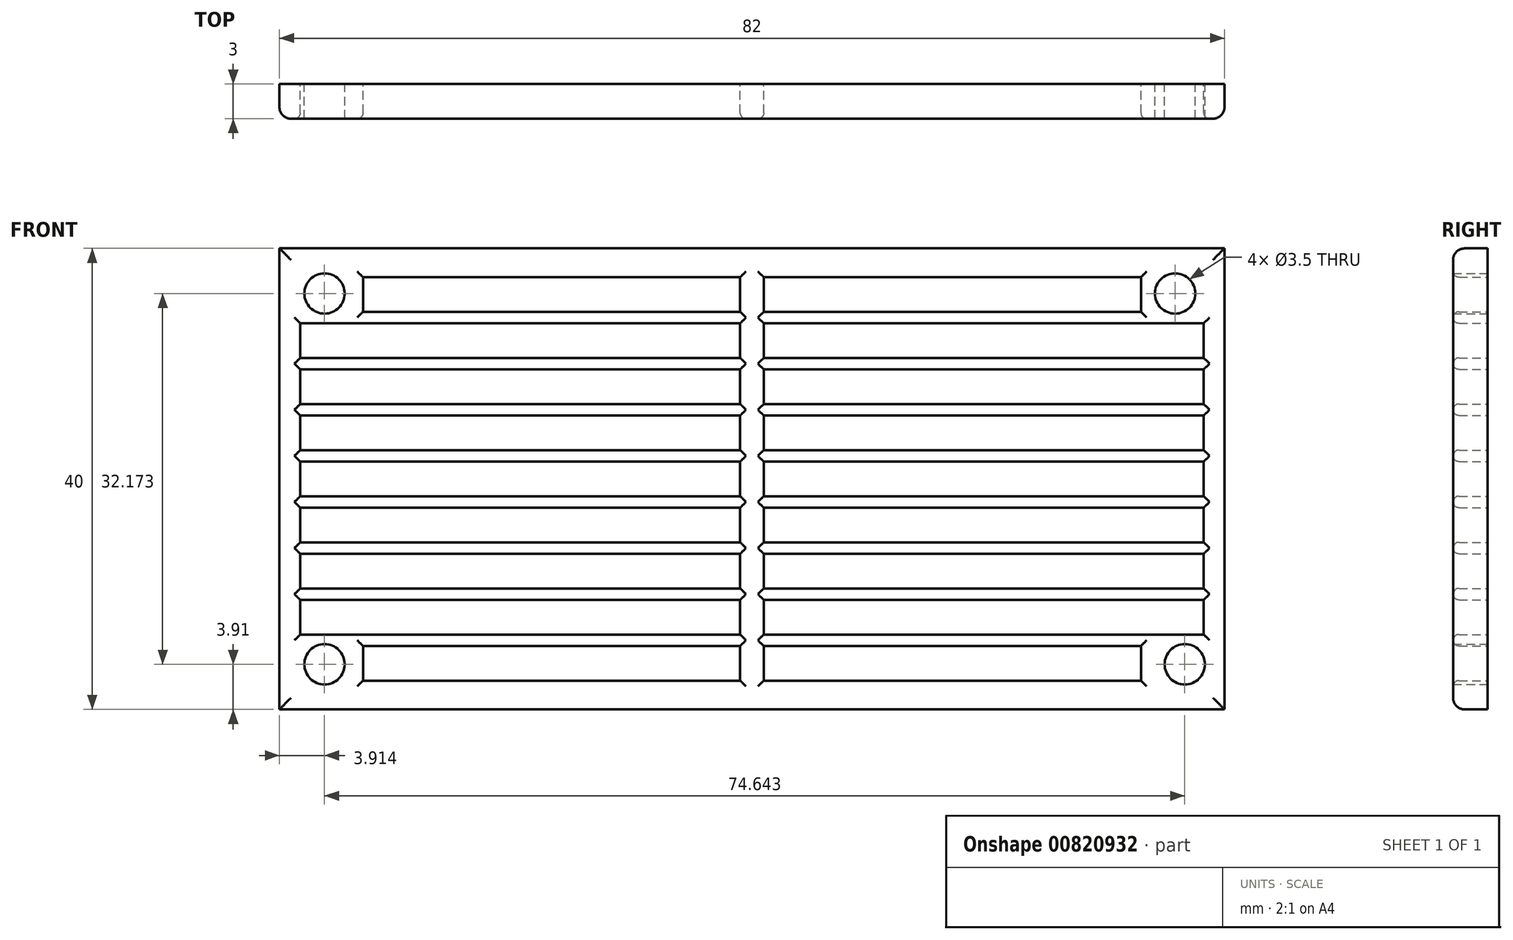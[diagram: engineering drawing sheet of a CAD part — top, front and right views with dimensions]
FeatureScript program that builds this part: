
annotation { "Feature Type Name" : "Feature", "Feature Type Description" : "" }
export const myFeature = defineFeature(function(context is Context, id is Id, definition is map)
    precondition{}
    {
        {
            var Q0;
            Q0=qCreatedBy(makeId("Front.planeOp"),FACE);
            var sketch = newSketch(context, id + "F0", { "sketchPlane" : qUnion([Q0])});
            skLineSegment(sketch, "E0.bottom", {"start": v(-95.77, 58.49) * mm, "end": v(-55.77, 58.49) * mm, "construction": true});
            skLineSegment(sketch, "E0.top", {"start": v(-95.77, 18.49) * mm, "end": v(-55.77, 18.49) * mm, "construction": true});
            skLineSegment(sketch, "E0.left", {"start": v(-95.77, 58.49) * mm, "end": v(-95.77, 18.49) * mm, "construction": true});
            skPoint(sketch, "E0.middle", {"position": v(-75.77, 38.49) * mm});
            skLineSegment(sketch, "E1.left", {"start": v(-13.77, 58.96) * mm, "end": v(-13.77, 18.96) * mm, "construction": true});
            skPoint(sketch, "E1.middle", {"position": v(-33.77, 38.49) * mm});
            skCircle(sketch, "E2", {"center": v(-91.86, 54.57) * mm, "radius": 1.75 * mm});
            skCircle(sketch, "E3", {"center": v(-91.86, 22.4) * mm, "radius": 1.75 * mm});
            skCircle(sketch, "E4", {"center": v(-18.05, 54.57) * mm, "radius": 1.75 * mm});
            skCircle(sketch, "E5", {"center": v(-17.21, 22.4) * mm, "radius": 1.75 * mm});
            skPoint(sketch, "E6.middle", {"position": v(-54.77, 38.49) * mm});
            skPoint(sketch, "E7.centerSnap0", {"position": v(-13.77, 38.96) * mm});
            skLineSegment(sketch, "E8.bottom", {"start": v(-95.77, 58.49) * mm, "end": v(-13.77, 58.49) * mm});
            skLineSegment(sketch, "E8.top", {"start": v(-95.77, 18.49) * mm, "end": v(-13.77, 18.49) * mm});
            skLineSegment(sketch, "E8.left", {"start": v(-95.77, 58.49) * mm, "end": v(-95.77, 18.49) * mm});
            skLineSegment(sketch, "E8.right", {"start": v(-13.77, 58.49) * mm, "end": v(-13.77, 18.49) * mm});
            skLineSegment(sketch, "E9.bottom", {"start": v(-15.57, 39.99) * mm, "end": v(-93.96, 39.99) * mm});
            skLineSegment(sketch, "E9.top", {"start": v(-15.57, 36.99) * mm, "end": v(-93.96, 36.99) * mm});
            skLineSegment(sketch, "E9.left", {"start": v(-15.57, 39.99) * mm, "end": v(-15.57, 36.99) * mm});
            skLineSegment(sketch, "E9.right", {"start": v(-93.96, 39.99) * mm, "end": v(-93.96, 36.99) * mm});
            skLineSegment(sketch, "E10.bottom", {"start": v(-15.57, 35.99) * mm, "end": v(-93.96, 35.99) * mm});
            skLineSegment(sketch, "E10.top", {"start": v(-15.57, 32.99) * mm, "end": v(-93.96, 32.99) * mm});
            skLineSegment(sketch, "E10.left", {"start": v(-15.57, 35.99) * mm, "end": v(-15.57, 32.99) * mm});
            skLineSegment(sketch, "E10.right", {"start": v(-93.96, 35.99) * mm, "end": v(-93.96, 32.99) * mm});
            skPoint(sketch, "E10.middle", {"position": v(-54.77, 34.49) * mm});
            skPoint(sketch, "E10.middle.positionSnap0", {"position": v(-54.77, 36.99) * mm});
            skPoint(sketch, "E10.centerSnap0", {"position": v(-54.77, 36.99) * mm});
            skLineSegment(sketch, "E11.bottom", {"start": v(-15.57, 31.99) * mm, "end": v(-93.96, 31.99) * mm});
            skLineSegment(sketch, "E11.top", {"start": v(-15.57, 28.99) * mm, "end": v(-93.96, 28.99) * mm});
            skLineSegment(sketch, "E11.left", {"start": v(-15.57, 31.99) * mm, "end": v(-15.57, 28.99) * mm});
            skLineSegment(sketch, "E11.right", {"start": v(-93.96, 31.99) * mm, "end": v(-93.96, 28.99) * mm});
            skPoint(sketch, "E11.middle", {"position": v(-54.77, 30.49) * mm});
            skPoint(sketch, "E11.middle.positionSnap0", {"position": v(-54.77, 32.99) * mm});
            skPoint(sketch, "E11.centerSnap0", {"position": v(-54.77, 32.99) * mm});
            skLineSegment(sketch, "E12.bottom", {"start": v(-15.57, 27.99) * mm, "end": v(-93.96, 27.99) * mm});
            skLineSegment(sketch, "E12.top", {"start": v(-15.57, 24.99) * mm, "end": v(-93.96, 24.99) * mm});
            skLineSegment(sketch, "E12.left", {"start": v(-15.57, 27.99) * mm, "end": v(-15.57, 24.99) * mm});
            skLineSegment(sketch, "E12.right", {"start": v(-93.96, 27.99) * mm, "end": v(-93.96, 24.99) * mm});
            skPoint(sketch, "E12.middle", {"position": v(-54.77, 26.49) * mm});
            skPoint(sketch, "E12.middle.positionSnap0", {"position": v(-54.77, 28.99) * mm});
            skPoint(sketch, "E12.centerSnap0", {"position": v(-54.77, 28.99) * mm});
            skLineSegment(sketch, "E13.bottom", {"start": v(-15.57, 40.99) * mm, "end": v(-93.96, 40.99) * mm});
            skLineSegment(sketch, "E13.top", {"start": v(-15.57, 43.99) * mm, "end": v(-93.96, 43.99) * mm});
            skLineSegment(sketch, "E13.left", {"start": v(-15.57, 40.99) * mm, "end": v(-15.57, 43.99) * mm});
            skLineSegment(sketch, "E13.right", {"start": v(-93.96, 40.99) * mm, "end": v(-93.96, 43.99) * mm});
            skPoint(sketch, "E13.middle", {"position": v(-54.77, 42.49) * mm});
            skLineSegment(sketch, "E14.bottom", {"start": v(-15.57, 44.99) * mm, "end": v(-93.96, 44.99) * mm});
            skLineSegment(sketch, "E14.top", {"start": v(-15.57, 47.99) * mm, "end": v(-93.96, 47.99) * mm});
            skLineSegment(sketch, "E14.left", {"start": v(-15.57, 44.99) * mm, "end": v(-15.57, 47.99) * mm});
            skLineSegment(sketch, "E14.right", {"start": v(-93.96, 44.99) * mm, "end": v(-93.96, 47.99) * mm});
            skPoint(sketch, "E14.middle", {"position": v(-54.77, 46.49) * mm});
            skPoint(sketch, "E14.middle.positionSnap0", {"position": v(-54.77, 43.99) * mm});
            skPoint(sketch, "E14.centerSnap0", {"position": v(-54.77, 43.99) * mm});
            skLineSegment(sketch, "E15.bottom", {"start": v(-15.57, 48.99) * mm, "end": v(-93.96, 48.99) * mm});
            skLineSegment(sketch, "E15.top", {"start": v(-15.57, 51.99) * mm, "end": v(-93.96, 51.99) * mm});
            skLineSegment(sketch, "E15.left", {"start": v(-15.57, 48.99) * mm, "end": v(-15.57, 51.99) * mm});
            skLineSegment(sketch, "E15.right", {"start": v(-93.96, 48.99) * mm, "end": v(-93.96, 51.99) * mm});
            skPoint(sketch, "E15.middle", {"position": v(-54.77, 50.49) * mm});
            skLineSegment(sketch, "E16.bottom", {"start": v(-21.02, 52.99) * mm, "end": v(-88.52, 52.99) * mm});
            skLineSegment(sketch, "E16.top", {"start": v(-21.02, 55.99) * mm, "end": v(-88.52, 55.99) * mm});
            skLineSegment(sketch, "E16.left", {"start": v(-21.02, 52.99) * mm, "end": v(-21.02, 55.99) * mm});
            skLineSegment(sketch, "E16.right", {"start": v(-88.52, 52.99) * mm, "end": v(-88.52, 55.99) * mm});
            skPoint(sketch, "E16.middle", {"position": v(-54.77, 54.49) * mm});
            skLineSegment(sketch, "E17.bottom", {"start": v(-21.02, 20.99) * mm, "end": v(-88.52, 20.99) * mm});
            skLineSegment(sketch, "E17.top", {"start": v(-21.02, 23.99) * mm, "end": v(-88.52, 23.99) * mm});
            skLineSegment(sketch, "E17.left", {"start": v(-21.02, 20.99) * mm, "end": v(-21.02, 23.99) * mm});
            skLineSegment(sketch, "E17.right", {"start": v(-88.52, 20.99) * mm, "end": v(-88.52, 23.99) * mm});
            skPoint(sketch, "E17.middle", {"position": v(-54.77, 22.49) * mm});
            skPoint(sketch, "E17.middle.positionSnap0", {"position": v(-54.77, 24.99) * mm});
            skPoint(sketch, "E17.centerSnap0", {"position": v(-54.77, 24.99) * mm});
            skLineSegment(sketch, "E18.bottom", {"start": v(-53.74, 20.99) * mm, "end": v(-55.8, 20.99) * mm});
            skLineSegment(sketch, "E18.top", {"start": v(-53.74, 55.99) * mm, "end": v(-55.8, 55.99) * mm});
            skLineSegment(sketch, "E18.left", {"start": v(-53.74, 20.99) * mm, "end": v(-53.74, 55.99) * mm});
            skLineSegment(sketch, "E18.right", {"start": v(-55.8, 20.99) * mm, "end": v(-55.8, 55.99) * mm});
            skSolve(sketch);
        }
        {
            var Q0;
            Q0=makeQuery(id+"F0.imprint","IMPRINT",FACE,{"disambiguationData":[TD([[makeQuery(id+"F0.imprint","IMPRINT",EDGE,{"derivedFrom":sQuery(id+"F0.wireOp",EDGE,"E2")}),-1.0]])]});
            var Q1;
            {var subQ0=sQuery(id+"F0.wireOp",EDGE,"E18.right");var subQ1=sQuery(id+"F0.wireOp",EDGE,"E16.bottom");var subQ2=makeQuery(id+"F0.imprint","INTERSECT",VERTEX,{"derivedFrom":[subQ1,subQ0]});Q1=makeQuery(id+"F0.imprint","IMPRINT",FACE,{"disambiguationData":[TD([[makeQuery(id+"F0.imprint","IMPRINT",EDGE,{"disambiguationData":[TD([[subQ2,1.0]])],"derivedFrom":subQ1}),-1.0]])]});}
            var Q2;
            {var subQ0=sQuery(id+"F0.wireOp",EDGE,"E18.right");var subQ1=sQuery(id+"F0.wireOp",EDGE,"E15.top");var subQ2=makeQuery(id+"F0.imprint","INTERSECT",VERTEX,{"derivedFrom":[subQ1,subQ0]});Q2=makeQuery(id+"F0.imprint","IMPRINT",FACE,{"disambiguationData":[TD([[makeQuery(id+"F0.imprint","IMPRINT",EDGE,{"disambiguationData":[TD([[subQ2,1.0]])],"derivedFrom":subQ1}),-1.0]])]});}
            var Q3;
            {var subQ0=sQuery(id+"F0.wireOp",EDGE,"E18.right");var subQ1=sQuery(id+"F0.wireOp",EDGE,"E15.bottom");var subQ2=makeQuery(id+"F0.imprint","INTERSECT",VERTEX,{"derivedFrom":[subQ1,subQ0]});Q3=makeQuery(id+"F0.imprint","IMPRINT",FACE,{"disambiguationData":[TD([[makeQuery(id+"F0.imprint","IMPRINT",EDGE,{"disambiguationData":[TD([[subQ2,1.0]])],"derivedFrom":subQ1}),-1.0]])]});}
            var Q4;
            {var subQ0=sQuery(id+"F0.wireOp",EDGE,"E18.right");var subQ1=sQuery(id+"F0.wireOp",EDGE,"E14.top");var subQ2=makeQuery(id+"F0.imprint","INTERSECT",VERTEX,{"derivedFrom":[subQ1,subQ0]});Q4=makeQuery(id+"F0.imprint","IMPRINT",FACE,{"disambiguationData":[TD([[makeQuery(id+"F0.imprint","IMPRINT",EDGE,{"disambiguationData":[TD([[subQ2,1.0]])],"derivedFrom":subQ1}),-1.0]])]});}
            var Q5;
            {var subQ0=sQuery(id+"F0.wireOp",EDGE,"E18.right");var subQ1=sQuery(id+"F0.wireOp",EDGE,"E14.bottom");var subQ2=makeQuery(id+"F0.imprint","INTERSECT",VERTEX,{"derivedFrom":[subQ1,subQ0]});Q5=makeQuery(id+"F0.imprint","IMPRINT",FACE,{"disambiguationData":[TD([[makeQuery(id+"F0.imprint","IMPRINT",EDGE,{"disambiguationData":[TD([[subQ2,1.0]])],"derivedFrom":subQ1}),-1.0]])]});}
            var Q6;
            {var subQ0=sQuery(id+"F0.wireOp",EDGE,"E18.right");var subQ1=sQuery(id+"F0.wireOp",EDGE,"E13.top");var subQ2=makeQuery(id+"F0.imprint","INTERSECT",VERTEX,{"derivedFrom":[subQ1,subQ0]});Q6=makeQuery(id+"F0.imprint","IMPRINT",FACE,{"disambiguationData":[TD([[makeQuery(id+"F0.imprint","IMPRINT",EDGE,{"disambiguationData":[TD([[subQ2,1.0]])],"derivedFrom":subQ1}),-1.0]])]});}
            var Q7;
            {var subQ0=sQuery(id+"F0.wireOp",EDGE,"E18.right");var subQ1=sQuery(id+"F0.wireOp",EDGE,"E13.bottom");var subQ2=makeQuery(id+"F0.imprint","INTERSECT",VERTEX,{"derivedFrom":[subQ1,subQ0]});Q7=makeQuery(id+"F0.imprint","IMPRINT",FACE,{"disambiguationData":[TD([[makeQuery(id+"F0.imprint","IMPRINT",EDGE,{"disambiguationData":[TD([[subQ2,1.0]])],"derivedFrom":subQ1}),-1.0]])]});}
            var Q8;
            {var subQ0=sQuery(id+"F0.wireOp",EDGE,"E18.right");var subQ1=sQuery(id+"F0.wireOp",EDGE,"E9.bottom");var subQ2=makeQuery(id+"F0.imprint","INTERSECT",VERTEX,{"derivedFrom":[subQ1,subQ0]});Q8=makeQuery(id+"F0.imprint","IMPRINT",FACE,{"disambiguationData":[TD([[makeQuery(id+"F0.imprint","IMPRINT",EDGE,{"disambiguationData":[TD([[subQ2,1.0]])],"derivedFrom":subQ1}),-1.0]])]});}
            var Q9;
            {var subQ0=sQuery(id+"F0.wireOp",EDGE,"E18.right");var subQ1=sQuery(id+"F0.wireOp",EDGE,"E9.bottom");var subQ2=makeQuery(id+"F0.imprint","INTERSECT",VERTEX,{"derivedFrom":[subQ1,subQ0]});Q9=makeQuery(id+"F0.imprint","IMPRINT",FACE,{"disambiguationData":[TD([[makeQuery(id+"F0.imprint","IMPRINT",EDGE,{"disambiguationData":[TD([[subQ2,1.0]])],"derivedFrom":subQ1}),1.0]])]});}
            var Q10;
            {var subQ0=sQuery(id+"F0.wireOp",EDGE,"E18.right");var subQ1=sQuery(id+"F0.wireOp",EDGE,"E9.top");var subQ2=makeQuery(id+"F0.imprint","INTERSECT",VERTEX,{"derivedFrom":[subQ1,subQ0]});Q10=makeQuery(id+"F0.imprint","IMPRINT",FACE,{"disambiguationData":[TD([[makeQuery(id+"F0.imprint","IMPRINT",EDGE,{"disambiguationData":[TD([[subQ2,1.0]])],"derivedFrom":subQ1}),1.0]])]});}
            var Q11;
            {var subQ0=sQuery(id+"F0.wireOp",EDGE,"E18.right");var subQ1=sQuery(id+"F0.wireOp",EDGE,"E10.bottom");var subQ2=makeQuery(id+"F0.imprint","INTERSECT",VERTEX,{"derivedFrom":[subQ1,subQ0]});Q11=makeQuery(id+"F0.imprint","IMPRINT",FACE,{"disambiguationData":[TD([[makeQuery(id+"F0.imprint","IMPRINT",EDGE,{"disambiguationData":[TD([[subQ2,1.0]])],"derivedFrom":subQ1}),1.0]])]});}
            var Q12;
            {var subQ0=sQuery(id+"F0.wireOp",EDGE,"E18.right");var subQ1=sQuery(id+"F0.wireOp",EDGE,"E10.top");var subQ2=makeQuery(id+"F0.imprint","INTERSECT",VERTEX,{"derivedFrom":[subQ1,subQ0]});Q12=makeQuery(id+"F0.imprint","IMPRINT",FACE,{"disambiguationData":[TD([[makeQuery(id+"F0.imprint","IMPRINT",EDGE,{"disambiguationData":[TD([[subQ2,1.0]])],"derivedFrom":subQ1}),1.0]])]});}
            var Q13;
            {var subQ0=sQuery(id+"F0.wireOp",EDGE,"E18.right");var subQ1=sQuery(id+"F0.wireOp",EDGE,"E11.bottom");var subQ2=makeQuery(id+"F0.imprint","INTERSECT",VERTEX,{"derivedFrom":[subQ1,subQ0]});Q13=makeQuery(id+"F0.imprint","IMPRINT",FACE,{"disambiguationData":[TD([[makeQuery(id+"F0.imprint","IMPRINT",EDGE,{"disambiguationData":[TD([[subQ2,1.0]])],"derivedFrom":subQ1}),1.0]])]});}
            var Q14;
            {var subQ0=sQuery(id+"F0.wireOp",EDGE,"E18.right");var subQ1=sQuery(id+"F0.wireOp",EDGE,"E11.top");var subQ2=makeQuery(id+"F0.imprint","INTERSECT",VERTEX,{"derivedFrom":[subQ1,subQ0]});Q14=makeQuery(id+"F0.imprint","IMPRINT",FACE,{"disambiguationData":[TD([[makeQuery(id+"F0.imprint","IMPRINT",EDGE,{"disambiguationData":[TD([[subQ2,1.0]])],"derivedFrom":subQ1}),1.0]])]});}
            var Q15;
            {var subQ0=sQuery(id+"F0.wireOp",EDGE,"E18.right");var subQ1=sQuery(id+"F0.wireOp",EDGE,"E12.bottom");var subQ2=makeQuery(id+"F0.imprint","INTERSECT",VERTEX,{"derivedFrom":[subQ1,subQ0]});Q15=makeQuery(id+"F0.imprint","IMPRINT",FACE,{"disambiguationData":[TD([[makeQuery(id+"F0.imprint","IMPRINT",EDGE,{"disambiguationData":[TD([[subQ2,1.0]])],"derivedFrom":subQ1}),1.0]])]});}
            var Q16;
            {var subQ0=sQuery(id+"F0.wireOp",EDGE,"E18.right");var subQ1=sQuery(id+"F0.wireOp",EDGE,"E12.top");var subQ2=makeQuery(id+"F0.imprint","INTERSECT",VERTEX,{"derivedFrom":[subQ1,subQ0]});Q16=makeQuery(id+"F0.imprint","IMPRINT",FACE,{"disambiguationData":[TD([[makeQuery(id+"F0.imprint","IMPRINT",EDGE,{"disambiguationData":[TD([[subQ2,1.0]])],"derivedFrom":subQ1}),1.0]])]});}
            var Q17;
            {var subQ0=sQuery(id+"F0.wireOp",EDGE,"E18.right");var subQ1=sQuery(id+"F0.wireOp",EDGE,"E17.bottom");var subQ2=makeQuery(id+"F0.imprint","INTERSECT",VERTEX,{"derivedFrom":[subQ1,subQ0]});Q17=makeQuery(id+"F0.imprint","IMPRINT",FACE,{"disambiguationData":[TD([[makeQuery(id+"F0.imprint","IMPRINT",EDGE,{"disambiguationData":[TD([[subQ2,1.0]])],"derivedFrom":subQ1}),-1.0]])]});}
            extrude(context, id + "F1", {"entities" : qUnion([Q0, Q1, Q2, Q3, Q4, Q5, Q6, Q7, Q8, Q9, Q10, Q11, Q12, Q13, Q14, Q15, Q16, Q17]), "depth" : 3 * mm, "offsetDistance" : 25 * mm});
        }
        {
            var Q0;
            {var subQ0=sQuery(id+"F0.wireOp",EDGE,"E17.bottom");Q0=makeQuery(id+"F1.opExtrude","CAP_EDGE",EDGE,{"disambiguationData":[OSD([subQ0]),TDD([makeQuery(id+"F0.imprint","IMPRINT",EDGE,{"disambiguationData":[TD([[makeQuery(id+"F0.imprint","INTERSECT",VERTEX,{"derivedFrom":[subQ0,sQuery(id+"F0.wireOp",EDGE,"E18.right")]}),-1.0]])],"derivedFrom":subQ0})])],"isStart":false});}
            var Q1;
            {var subQ0=sQuery(id+"F0.wireOp",EDGE,"E17.top");Q1=makeQuery(id+"F1.opExtrude","CAP_EDGE",EDGE,{"disambiguationData":[OSD([subQ0]),TDD([makeQuery(id+"F0.imprint","IMPRINT",EDGE,{"disambiguationData":[TD([[makeQuery(id+"F0.imprint","INTERSECT",VERTEX,{"derivedFrom":[subQ0,sQuery(id+"F0.wireOp",EDGE,"E18.right")]}),-1.0]])],"derivedFrom":subQ0})])],"isStart":false});}
            var Q2;
            {var subQ0=sQuery(id+"F0.wireOp",EDGE,"E12.top");Q2=makeQuery(id+"F1.opExtrude","CAP_EDGE",EDGE,{"disambiguationData":[OSD([subQ0]),TDD([makeQuery(id+"F0.imprint","IMPRINT",EDGE,{"disambiguationData":[TD([[makeQuery(id+"F0.imprint","INTERSECT",VERTEX,{"derivedFrom":[subQ0,sQuery(id+"F0.wireOp",EDGE,"E18.right")]}),-1.0]])],"derivedFrom":subQ0})])],"isStart":false});}
            var Q3;
            {var subQ0=sQuery(id+"F0.wireOp",EDGE,"E12.bottom");Q3=makeQuery(id+"F1.opExtrude","CAP_EDGE",EDGE,{"disambiguationData":[OSD([subQ0]),TDD([makeQuery(id+"F0.imprint","IMPRINT",EDGE,{"disambiguationData":[TD([[makeQuery(id+"F0.imprint","INTERSECT",VERTEX,{"derivedFrom":[subQ0,sQuery(id+"F0.wireOp",EDGE,"E18.right")]}),-1.0]])],"derivedFrom":subQ0})])],"isStart":false});}
            var Q4;
            {var subQ0=sQuery(id+"F0.wireOp",EDGE,"E11.top");Q4=makeQuery(id+"F1.opExtrude","CAP_EDGE",EDGE,{"disambiguationData":[OSD([subQ0]),TDD([makeQuery(id+"F0.imprint","IMPRINT",EDGE,{"disambiguationData":[TD([[makeQuery(id+"F0.imprint","INTERSECT",VERTEX,{"derivedFrom":[subQ0,sQuery(id+"F0.wireOp",EDGE,"E18.right")]}),-1.0]])],"derivedFrom":subQ0})])],"isStart":false});}
            var Q5;
            {var subQ0=sQuery(id+"F0.wireOp",EDGE,"E11.bottom");Q5=makeQuery(id+"F1.opExtrude","CAP_EDGE",EDGE,{"disambiguationData":[OSD([subQ0]),TDD([makeQuery(id+"F0.imprint","IMPRINT",EDGE,{"disambiguationData":[TD([[makeQuery(id+"F0.imprint","INTERSECT",VERTEX,{"derivedFrom":[subQ0,sQuery(id+"F0.wireOp",EDGE,"E18.right")]}),-1.0]])],"derivedFrom":subQ0})])],"isStart":false});}
            var Q6;
            {var subQ0=sQuery(id+"F0.wireOp",EDGE,"E10.top");Q6=makeQuery(id+"F1.opExtrude","CAP_EDGE",EDGE,{"disambiguationData":[OSD([subQ0]),TDD([makeQuery(id+"F0.imprint","IMPRINT",EDGE,{"disambiguationData":[TD([[makeQuery(id+"F0.imprint","INTERSECT",VERTEX,{"derivedFrom":[subQ0,sQuery(id+"F0.wireOp",EDGE,"E18.right")]}),-1.0]])],"derivedFrom":subQ0})])],"isStart":false});}
            var Q7;
            {var subQ0=sQuery(id+"F0.wireOp",EDGE,"E10.bottom");Q7=makeQuery(id+"F1.opExtrude","CAP_EDGE",EDGE,{"disambiguationData":[OSD([subQ0]),TDD([makeQuery(id+"F0.imprint","IMPRINT",EDGE,{"disambiguationData":[TD([[makeQuery(id+"F0.imprint","INTERSECT",VERTEX,{"derivedFrom":[subQ0,sQuery(id+"F0.wireOp",EDGE,"E18.right")]}),-1.0]])],"derivedFrom":subQ0})])],"isStart":false});}
            var Q8;
            {var subQ0=sQuery(id+"F0.wireOp",EDGE,"E9.top");Q8=makeQuery(id+"F1.opExtrude","CAP_EDGE",EDGE,{"disambiguationData":[OSD([subQ0]),TDD([makeQuery(id+"F0.imprint","IMPRINT",EDGE,{"disambiguationData":[TD([[makeQuery(id+"F0.imprint","INTERSECT",VERTEX,{"derivedFrom":[subQ0,sQuery(id+"F0.wireOp",EDGE,"E18.right")]}),-1.0]])],"derivedFrom":subQ0})])],"isStart":false});}
            var Q9;
            {var subQ0=sQuery(id+"F0.wireOp",EDGE,"E17.bottom");Q9=makeQuery(id+"F1.opExtrude","CAP_EDGE",EDGE,{"disambiguationData":[OSD([subQ0]),TDD([makeQuery(id+"F0.imprint","IMPRINT",EDGE,{"disambiguationData":[TD([[makeQuery(id+"F0.imprint","INTERSECT",VERTEX,{"derivedFrom":[subQ0,sQuery(id+"F0.wireOp",EDGE,"E17.left")]}),-1.0]])],"derivedFrom":subQ0})])],"isStart":false});}
            var Q10;
            {var subQ0=sQuery(id+"F0.wireOp",EDGE,"E17.top");Q10=makeQuery(id+"F1.opExtrude","CAP_EDGE",EDGE,{"disambiguationData":[OSD([subQ0]),TDD([makeQuery(id+"F0.imprint","IMPRINT",EDGE,{"disambiguationData":[TD([[makeQuery(id+"F0.imprint","INTERSECT",VERTEX,{"derivedFrom":[subQ0,sQuery(id+"F0.wireOp",EDGE,"E17.left")]}),-1.0]])],"derivedFrom":subQ0})])],"isStart":false});}
            var Q11;
            {var subQ0=sQuery(id+"F0.wireOp",EDGE,"E12.top");Q11=makeQuery(id+"F1.opExtrude","CAP_EDGE",EDGE,{"disambiguationData":[OSD([subQ0]),TDD([makeQuery(id+"F0.imprint","IMPRINT",EDGE,{"disambiguationData":[TD([[makeQuery(id+"F0.imprint","INTERSECT",VERTEX,{"derivedFrom":[subQ0,sQuery(id+"F0.wireOp",EDGE,"E12.left")]}),-1.0]])],"derivedFrom":subQ0})])],"isStart":false});}
            var Q12;
            {var subQ0=sQuery(id+"F0.wireOp",EDGE,"E12.bottom");Q12=makeQuery(id+"F1.opExtrude","CAP_EDGE",EDGE,{"disambiguationData":[OSD([subQ0]),TDD([makeQuery(id+"F0.imprint","IMPRINT",EDGE,{"disambiguationData":[TD([[makeQuery(id+"F0.imprint","INTERSECT",VERTEX,{"derivedFrom":[subQ0,sQuery(id+"F0.wireOp",EDGE,"E12.left")]}),-1.0]])],"derivedFrom":subQ0})])],"isStart":false});}
            var Q13;
            {var subQ0=sQuery(id+"F0.wireOp",EDGE,"E11.top");Q13=makeQuery(id+"F1.opExtrude","CAP_EDGE",EDGE,{"disambiguationData":[OSD([subQ0]),TDD([makeQuery(id+"F0.imprint","IMPRINT",EDGE,{"disambiguationData":[TD([[makeQuery(id+"F0.imprint","INTERSECT",VERTEX,{"derivedFrom":[subQ0,sQuery(id+"F0.wireOp",EDGE,"E11.left")]}),-1.0]])],"derivedFrom":subQ0})])],"isStart":false});}
            var Q14;
            {var subQ0=sQuery(id+"F0.wireOp",EDGE,"E11.bottom");Q14=makeQuery(id+"F1.opExtrude","CAP_EDGE",EDGE,{"disambiguationData":[OSD([subQ0]),TDD([makeQuery(id+"F0.imprint","IMPRINT",EDGE,{"disambiguationData":[TD([[makeQuery(id+"F0.imprint","INTERSECT",VERTEX,{"derivedFrom":[subQ0,sQuery(id+"F0.wireOp",EDGE,"E11.left")]}),-1.0]])],"derivedFrom":subQ0})])],"isStart":false});}
            var Q15;
            {var subQ0=sQuery(id+"F0.wireOp",EDGE,"E10.top");Q15=makeQuery(id+"F1.opExtrude","CAP_EDGE",EDGE,{"disambiguationData":[OSD([subQ0]),TDD([makeQuery(id+"F0.imprint","IMPRINT",EDGE,{"disambiguationData":[TD([[makeQuery(id+"F0.imprint","INTERSECT",VERTEX,{"derivedFrom":[subQ0,sQuery(id+"F0.wireOp",EDGE,"E10.left")]}),-1.0]])],"derivedFrom":subQ0})])],"isStart":false});}
            var Q16;
            {var subQ0=sQuery(id+"F0.wireOp",EDGE,"E10.bottom");Q16=makeQuery(id+"F1.opExtrude","CAP_EDGE",EDGE,{"disambiguationData":[OSD([subQ0]),TDD([makeQuery(id+"F0.imprint","IMPRINT",EDGE,{"disambiguationData":[TD([[makeQuery(id+"F0.imprint","INTERSECT",VERTEX,{"derivedFrom":[subQ0,sQuery(id+"F0.wireOp",EDGE,"E10.left")]}),-1.0]])],"derivedFrom":subQ0})])],"isStart":false});}
            var Q17;
            {var subQ0=sQuery(id+"F0.wireOp",EDGE,"E9.top");Q17=makeQuery(id+"F1.opExtrude","CAP_EDGE",EDGE,{"disambiguationData":[OSD([subQ0]),TDD([makeQuery(id+"F0.imprint","IMPRINT",EDGE,{"disambiguationData":[TD([[makeQuery(id+"F0.imprint","INTERSECT",VERTEX,{"derivedFrom":[subQ0,sQuery(id+"F0.wireOp",EDGE,"E9.left")]}),-1.0]])],"derivedFrom":subQ0})])],"isStart":false});}
            var Q18;
            {var subQ0=sQuery(id+"F0.wireOp",EDGE,"E9.bottom");Q18=makeQuery(id+"F1.opExtrude","CAP_EDGE",EDGE,{"disambiguationData":[OSD([subQ0]),TDD([makeQuery(id+"F0.imprint","IMPRINT",EDGE,{"disambiguationData":[TD([[makeQuery(id+"F0.imprint","INTERSECT",VERTEX,{"derivedFrom":[subQ0,sQuery(id+"F0.wireOp",EDGE,"E18.right")]}),-1.0]])],"derivedFrom":subQ0})])],"isStart":false});}
            var Q19;
            {var subQ0=sQuery(id+"F0.wireOp",EDGE,"E13.bottom");Q19=makeQuery(id+"F1.opExtrude","CAP_EDGE",EDGE,{"disambiguationData":[OSD([subQ0]),TDD([makeQuery(id+"F0.imprint","IMPRINT",EDGE,{"disambiguationData":[TD([[makeQuery(id+"F0.imprint","INTERSECT",VERTEX,{"derivedFrom":[subQ0,sQuery(id+"F0.wireOp",EDGE,"E18.right")]}),-1.0]])],"derivedFrom":subQ0})])],"isStart":false});}
            var Q20;
            {var subQ0=sQuery(id+"F0.wireOp",EDGE,"E13.top");Q20=makeQuery(id+"F1.opExtrude","CAP_EDGE",EDGE,{"disambiguationData":[OSD([subQ0]),TDD([makeQuery(id+"F0.imprint","IMPRINT",EDGE,{"disambiguationData":[TD([[makeQuery(id+"F0.imprint","INTERSECT",VERTEX,{"derivedFrom":[subQ0,sQuery(id+"F0.wireOp",EDGE,"E18.right")]}),-1.0]])],"derivedFrom":subQ0})])],"isStart":false});}
            var Q21;
            {var subQ0=sQuery(id+"F0.wireOp",EDGE,"E14.bottom");Q21=makeQuery(id+"F1.opExtrude","CAP_EDGE",EDGE,{"disambiguationData":[OSD([subQ0]),TDD([makeQuery(id+"F0.imprint","IMPRINT",EDGE,{"disambiguationData":[TD([[makeQuery(id+"F0.imprint","INTERSECT",VERTEX,{"derivedFrom":[subQ0,sQuery(id+"F0.wireOp",EDGE,"E18.right")]}),-1.0]])],"derivedFrom":subQ0})])],"isStart":false});}
            var Q22;
            {var subQ0=sQuery(id+"F0.wireOp",EDGE,"E14.top");Q22=makeQuery(id+"F1.opExtrude","CAP_EDGE",EDGE,{"disambiguationData":[OSD([subQ0]),TDD([makeQuery(id+"F0.imprint","IMPRINT",EDGE,{"disambiguationData":[TD([[makeQuery(id+"F0.imprint","INTERSECT",VERTEX,{"derivedFrom":[subQ0,sQuery(id+"F0.wireOp",EDGE,"E18.right")]}),-1.0]])],"derivedFrom":subQ0})])],"isStart":false});}
            var Q23;
            {var subQ0=sQuery(id+"F0.wireOp",EDGE,"E15.bottom");Q23=makeQuery(id+"F1.opExtrude","CAP_EDGE",EDGE,{"disambiguationData":[OSD([subQ0]),TDD([makeQuery(id+"F0.imprint","IMPRINT",EDGE,{"disambiguationData":[TD([[makeQuery(id+"F0.imprint","INTERSECT",VERTEX,{"derivedFrom":[subQ0,sQuery(id+"F0.wireOp",EDGE,"E18.right")]}),-1.0]])],"derivedFrom":subQ0})])],"isStart":false});}
            var Q24;
            {var subQ0=sQuery(id+"F0.wireOp",EDGE,"E15.top");Q24=makeQuery(id+"F1.opExtrude","CAP_EDGE",EDGE,{"disambiguationData":[OSD([subQ0]),TDD([makeQuery(id+"F0.imprint","IMPRINT",EDGE,{"disambiguationData":[TD([[makeQuery(id+"F0.imprint","INTERSECT",VERTEX,{"derivedFrom":[subQ0,sQuery(id+"F0.wireOp",EDGE,"E18.right")]}),-1.0]])],"derivedFrom":subQ0})])],"isStart":false});}
            var Q25;
            {var subQ0=sQuery(id+"F0.wireOp",EDGE,"E16.bottom");Q25=makeQuery(id+"F1.opExtrude","CAP_EDGE",EDGE,{"disambiguationData":[OSD([subQ0]),TDD([makeQuery(id+"F0.imprint","IMPRINT",EDGE,{"disambiguationData":[TD([[makeQuery(id+"F0.imprint","INTERSECT",VERTEX,{"derivedFrom":[subQ0,sQuery(id+"F0.wireOp",EDGE,"E18.right")]}),-1.0]])],"derivedFrom":subQ0})])],"isStart":false});}
            var Q26;
            Q26=makeQuery(id+"F1.opExtrude","CAP_EDGE",EDGE,{"disambiguationData":[OSD([sQuery(id+"F0.wireOp",EDGE,"E12.right")])],"isStart":false});
            var Q27;
            Q27=makeQuery(id+"F1.opExtrude","CAP_EDGE",EDGE,{"disambiguationData":[OSD([sQuery(id+"F0.wireOp",EDGE,"E11.right")])],"isStart":false});
            var Q28;
            Q28=makeQuery(id+"F1.opExtrude","CAP_EDGE",EDGE,{"disambiguationData":[OSD([sQuery(id+"F0.wireOp",EDGE,"E10.right")])],"isStart":false});
            var Q29;
            Q29=makeQuery(id+"F1.opExtrude","CAP_EDGE",EDGE,{"disambiguationData":[OSD([sQuery(id+"F0.wireOp",EDGE,"E17.right")])],"isStart":false});
            var Q30;
            {var subQ0=sQuery(id+"F0.wireOp",EDGE,"E18.right");Q30=makeQuery(id+"F1.opExtrude","CAP_EDGE",EDGE,{"disambiguationData":[OSD([subQ0]),TDD([makeQuery(id+"F0.imprint","IMPRINT",EDGE,{"disambiguationData":[TD([[makeQuery(id+"F0.imprint","INTERSECT",VERTEX,{"derivedFrom":[sQuery(id+"F0.wireOp",EDGE,"E17.bottom"),subQ0]}),-1.0]])],"derivedFrom":subQ0})])],"isStart":false});}
            var Q31;
            {var subQ0=sQuery(id+"F0.wireOp",EDGE,"E18.right");Q31=makeQuery(id+"F1.opExtrude","CAP_EDGE",EDGE,{"disambiguationData":[OSD([subQ0]),TDD([makeQuery(id+"F0.imprint","IMPRINT",EDGE,{"disambiguationData":[TD([[makeQuery(id+"F0.imprint","INTERSECT",VERTEX,{"derivedFrom":[sQuery(id+"F0.wireOp",EDGE,"E12.bottom"),subQ0]}),1.0]])],"derivedFrom":subQ0})])],"isStart":false});}
            var Q32;
            {var subQ0=sQuery(id+"F0.wireOp",EDGE,"E18.right");Q32=makeQuery(id+"F1.opExtrude","CAP_EDGE",EDGE,{"disambiguationData":[OSD([subQ0]),TDD([makeQuery(id+"F0.imprint","IMPRINT",EDGE,{"disambiguationData":[TD([[makeQuery(id+"F0.imprint","INTERSECT",VERTEX,{"derivedFrom":[sQuery(id+"F0.wireOp",EDGE,"E11.bottom"),subQ0]}),1.0]])],"derivedFrom":subQ0})])],"isStart":false});}
            var Q33;
            {var subQ0=sQuery(id+"F0.wireOp",EDGE,"E18.right");Q33=makeQuery(id+"F1.opExtrude","CAP_EDGE",EDGE,{"disambiguationData":[OSD([subQ0]),TDD([makeQuery(id+"F0.imprint","IMPRINT",EDGE,{"disambiguationData":[TD([[makeQuery(id+"F0.imprint","INTERSECT",VERTEX,{"derivedFrom":[sQuery(id+"F0.wireOp",EDGE,"E10.bottom"),subQ0]}),1.0]])],"derivedFrom":subQ0})])],"isStart":false});}
            var Q34;
            {var subQ0=sQuery(id+"F0.wireOp",EDGE,"E18.right");Q34=makeQuery(id+"F1.opExtrude","CAP_EDGE",EDGE,{"disambiguationData":[OSD([subQ0]),TDD([makeQuery(id+"F0.imprint","IMPRINT",EDGE,{"disambiguationData":[TD([[makeQuery(id+"F0.imprint","INTERSECT",VERTEX,{"derivedFrom":[sQuery(id+"F0.wireOp",EDGE,"E9.bottom"),subQ0]}),1.0]])],"derivedFrom":subQ0})])],"isStart":false});}
            var Q35;
            {var subQ0=sQuery(id+"F0.wireOp",EDGE,"E18.right");Q35=makeQuery(id+"F1.opExtrude","CAP_EDGE",EDGE,{"disambiguationData":[OSD([subQ0]),TDD([makeQuery(id+"F0.imprint","IMPRINT",EDGE,{"disambiguationData":[TD([[makeQuery(id+"F0.imprint","INTERSECT",VERTEX,{"derivedFrom":[sQuery(id+"F0.wireOp",EDGE,"E13.bottom"),subQ0]}),-1.0]])],"derivedFrom":subQ0})])],"isStart":false});}
            var Q36;
            {var subQ0=sQuery(id+"F0.wireOp",EDGE,"E18.right");Q36=makeQuery(id+"F1.opExtrude","CAP_EDGE",EDGE,{"disambiguationData":[OSD([subQ0]),TDD([makeQuery(id+"F0.imprint","IMPRINT",EDGE,{"disambiguationData":[TD([[makeQuery(id+"F0.imprint","INTERSECT",VERTEX,{"derivedFrom":[sQuery(id+"F0.wireOp",EDGE,"E14.bottom"),subQ0]}),-1.0]])],"derivedFrom":subQ0})])],"isStart":false});}
            var Q37;
            {var subQ0=sQuery(id+"F0.wireOp",EDGE,"E18.right");Q37=makeQuery(id+"F1.opExtrude","CAP_EDGE",EDGE,{"disambiguationData":[OSD([subQ0]),TDD([makeQuery(id+"F0.imprint","IMPRINT",EDGE,{"disambiguationData":[TD([[makeQuery(id+"F0.imprint","INTERSECT",VERTEX,{"derivedFrom":[sQuery(id+"F0.wireOp",EDGE,"E15.bottom"),subQ0]}),-1.0]])],"derivedFrom":subQ0})])],"isStart":false});}
            var Q38;
            {var subQ0=sQuery(id+"F0.wireOp",EDGE,"E18.right");Q38=makeQuery(id+"F1.opExtrude","CAP_EDGE",EDGE,{"disambiguationData":[OSD([subQ0]),TDD([makeQuery(id+"F0.imprint","IMPRINT",EDGE,{"disambiguationData":[TD([[makeQuery(id+"F0.imprint","INTERSECT",VERTEX,{"derivedFrom":[sQuery(id+"F0.wireOp",EDGE,"E16.bottom"),subQ0]}),-1.0]])],"derivedFrom":subQ0})])],"isStart":false});}
            var Q39;
            {var subQ0=sQuery(id+"F0.wireOp",EDGE,"E16.top");Q39=makeQuery(id+"F1.opExtrude","CAP_EDGE",EDGE,{"disambiguationData":[OSD([subQ0]),TDD([makeQuery(id+"F0.imprint","IMPRINT",EDGE,{"disambiguationData":[TD([[makeQuery(id+"F0.imprint","INTERSECT",VERTEX,{"derivedFrom":[subQ0,sQuery(id+"F0.wireOp",EDGE,"E18.right")]}),-1.0]])],"derivedFrom":subQ0})])],"isStart":false});}
            var Q40;
            {var subQ0=sQuery(id+"F0.wireOp",EDGE,"E18.left");Q40=makeQuery(id+"F1.opExtrude","CAP_EDGE",EDGE,{"disambiguationData":[OSD([subQ0]),TDD([makeQuery(id+"F0.imprint","IMPRINT",EDGE,{"disambiguationData":[TD([[makeQuery(id+"F0.imprint","INTERSECT",VERTEX,{"derivedFrom":[sQuery(id+"F0.wireOp",EDGE,"E17.bottom"),subQ0]}),-1.0]])],"derivedFrom":subQ0})])],"isStart":false});}
            var Q41;
            {var subQ0=sQuery(id+"F0.wireOp",EDGE,"E18.left");Q41=makeQuery(id+"F1.opExtrude","CAP_EDGE",EDGE,{"disambiguationData":[OSD([subQ0]),TDD([makeQuery(id+"F0.imprint","IMPRINT",EDGE,{"disambiguationData":[TD([[makeQuery(id+"F0.imprint","INTERSECT",VERTEX,{"derivedFrom":[sQuery(id+"F0.wireOp",EDGE,"E12.bottom"),subQ0]}),1.0]])],"derivedFrom":subQ0})])],"isStart":false});}
            var Q42;
            {var subQ0=sQuery(id+"F0.wireOp",EDGE,"E18.left");Q42=makeQuery(id+"F1.opExtrude","CAP_EDGE",EDGE,{"disambiguationData":[OSD([subQ0]),TDD([makeQuery(id+"F0.imprint","IMPRINT",EDGE,{"disambiguationData":[TD([[makeQuery(id+"F0.imprint","INTERSECT",VERTEX,{"derivedFrom":[sQuery(id+"F0.wireOp",EDGE,"E11.bottom"),subQ0]}),1.0]])],"derivedFrom":subQ0})])],"isStart":false});}
            var Q43;
            {var subQ0=sQuery(id+"F0.wireOp",EDGE,"E18.left");Q43=makeQuery(id+"F1.opExtrude","CAP_EDGE",EDGE,{"disambiguationData":[OSD([subQ0]),TDD([makeQuery(id+"F0.imprint","IMPRINT",EDGE,{"disambiguationData":[TD([[makeQuery(id+"F0.imprint","INTERSECT",VERTEX,{"derivedFrom":[sQuery(id+"F0.wireOp",EDGE,"E10.bottom"),subQ0]}),1.0]])],"derivedFrom":subQ0})])],"isStart":false});}
            var Q44;
            {var subQ0=sQuery(id+"F0.wireOp",EDGE,"E18.left");Q44=makeQuery(id+"F1.opExtrude","CAP_EDGE",EDGE,{"disambiguationData":[OSD([subQ0]),TDD([makeQuery(id+"F0.imprint","IMPRINT",EDGE,{"disambiguationData":[TD([[makeQuery(id+"F0.imprint","INTERSECT",VERTEX,{"derivedFrom":[sQuery(id+"F0.wireOp",EDGE,"E9.top"),subQ0]}),-1.0]])],"derivedFrom":subQ0})])],"isStart":false});}
            var Q45;
            {var subQ0=sQuery(id+"F0.wireOp",EDGE,"E9.bottom");Q45=makeQuery(id+"F1.opExtrude","CAP_EDGE",EDGE,{"disambiguationData":[OSD([subQ0]),TDD([makeQuery(id+"F0.imprint","IMPRINT",EDGE,{"disambiguationData":[TD([[makeQuery(id+"F0.imprint","INTERSECT",VERTEX,{"derivedFrom":[subQ0,sQuery(id+"F0.wireOp",EDGE,"E9.left")]}),-1.0]])],"derivedFrom":subQ0})])],"isStart":false});}
            var Q46;
            {var subQ0=sQuery(id+"F0.wireOp",EDGE,"E13.bottom");Q46=makeQuery(id+"F1.opExtrude","CAP_EDGE",EDGE,{"disambiguationData":[OSD([subQ0]),TDD([makeQuery(id+"F0.imprint","IMPRINT",EDGE,{"disambiguationData":[TD([[makeQuery(id+"F0.imprint","INTERSECT",VERTEX,{"derivedFrom":[subQ0,sQuery(id+"F0.wireOp",EDGE,"E13.left")]}),-1.0]])],"derivedFrom":subQ0})])],"isStart":false});}
            var Q47;
            {var subQ0=sQuery(id+"F0.wireOp",EDGE,"E18.left");Q47=makeQuery(id+"F1.opExtrude","CAP_EDGE",EDGE,{"disambiguationData":[OSD([subQ0]),TDD([makeQuery(id+"F0.imprint","IMPRINT",EDGE,{"disambiguationData":[TD([[makeQuery(id+"F0.imprint","INTERSECT",VERTEX,{"derivedFrom":[sQuery(id+"F0.wireOp",EDGE,"E13.bottom"),subQ0]}),-1.0]])],"derivedFrom":subQ0})])],"isStart":false});}
            var Q48;
            {var subQ0=sQuery(id+"F0.wireOp",EDGE,"E13.top");Q48=makeQuery(id+"F1.opExtrude","CAP_EDGE",EDGE,{"disambiguationData":[OSD([subQ0]),TDD([makeQuery(id+"F0.imprint","IMPRINT",EDGE,{"disambiguationData":[TD([[makeQuery(id+"F0.imprint","INTERSECT",VERTEX,{"derivedFrom":[subQ0,sQuery(id+"F0.wireOp",EDGE,"E13.left")]}),-1.0]])],"derivedFrom":subQ0})])],"isStart":false});}
            var Q49;
            {var subQ0=sQuery(id+"F0.wireOp",EDGE,"E14.bottom");Q49=makeQuery(id+"F1.opExtrude","CAP_EDGE",EDGE,{"disambiguationData":[OSD([subQ0]),TDD([makeQuery(id+"F0.imprint","IMPRINT",EDGE,{"disambiguationData":[TD([[makeQuery(id+"F0.imprint","INTERSECT",VERTEX,{"derivedFrom":[subQ0,sQuery(id+"F0.wireOp",EDGE,"E14.left")]}),-1.0]])],"derivedFrom":subQ0})])],"isStart":false});}
            var Q50;
            {var subQ0=sQuery(id+"F0.wireOp",EDGE,"E18.left");Q50=makeQuery(id+"F1.opExtrude","CAP_EDGE",EDGE,{"disambiguationData":[OSD([subQ0]),TDD([makeQuery(id+"F0.imprint","IMPRINT",EDGE,{"disambiguationData":[TD([[makeQuery(id+"F0.imprint","INTERSECT",VERTEX,{"derivedFrom":[sQuery(id+"F0.wireOp",EDGE,"E14.bottom"),subQ0]}),-1.0]])],"derivedFrom":subQ0})])],"isStart":false});}
            var Q51;
            {var subQ0=sQuery(id+"F0.wireOp",EDGE,"E15.bottom");Q51=makeQuery(id+"F1.opExtrude","CAP_EDGE",EDGE,{"disambiguationData":[OSD([subQ0]),TDD([makeQuery(id+"F0.imprint","IMPRINT",EDGE,{"disambiguationData":[TD([[makeQuery(id+"F0.imprint","INTERSECT",VERTEX,{"derivedFrom":[subQ0,sQuery(id+"F0.wireOp",EDGE,"E15.left")]}),-1.0]])],"derivedFrom":subQ0})])],"isStart":false});}
            var Q52;
            {var subQ0=sQuery(id+"F0.wireOp",EDGE,"E14.top");Q52=makeQuery(id+"F1.opExtrude","CAP_EDGE",EDGE,{"disambiguationData":[OSD([subQ0]),TDD([makeQuery(id+"F0.imprint","IMPRINT",EDGE,{"disambiguationData":[TD([[makeQuery(id+"F0.imprint","INTERSECT",VERTEX,{"derivedFrom":[subQ0,sQuery(id+"F0.wireOp",EDGE,"E14.left")]}),-1.0]])],"derivedFrom":subQ0})])],"isStart":false});}
            var Q53;
            {var subQ0=sQuery(id+"F0.wireOp",EDGE,"E18.left");Q53=makeQuery(id+"F1.opExtrude","CAP_EDGE",EDGE,{"disambiguationData":[OSD([subQ0]),TDD([makeQuery(id+"F0.imprint","IMPRINT",EDGE,{"disambiguationData":[TD([[makeQuery(id+"F0.imprint","INTERSECT",VERTEX,{"derivedFrom":[sQuery(id+"F0.wireOp",EDGE,"E15.bottom"),subQ0]}),-1.0]])],"derivedFrom":subQ0})])],"isStart":false});}
            var Q54;
            {var subQ0=sQuery(id+"F0.wireOp",EDGE,"E15.top");Q54=makeQuery(id+"F1.opExtrude","CAP_EDGE",EDGE,{"disambiguationData":[OSD([subQ0]),TDD([makeQuery(id+"F0.imprint","IMPRINT",EDGE,{"disambiguationData":[TD([[makeQuery(id+"F0.imprint","INTERSECT",VERTEX,{"derivedFrom":[subQ0,sQuery(id+"F0.wireOp",EDGE,"E15.left")]}),-1.0]])],"derivedFrom":subQ0})])],"isStart":false});}
            var Q55;
            {var subQ0=sQuery(id+"F0.wireOp",EDGE,"E16.bottom");Q55=makeQuery(id+"F1.opExtrude","CAP_EDGE",EDGE,{"disambiguationData":[OSD([subQ0]),TDD([makeQuery(id+"F0.imprint","IMPRINT",EDGE,{"disambiguationData":[TD([[makeQuery(id+"F0.imprint","INTERSECT",VERTEX,{"derivedFrom":[subQ0,sQuery(id+"F0.wireOp",EDGE,"E16.left")]}),-1.0]])],"derivedFrom":subQ0})])],"isStart":false});}
            var Q56;
            {var subQ0=sQuery(id+"F0.wireOp",EDGE,"E18.left");Q56=makeQuery(id+"F1.opExtrude","CAP_EDGE",EDGE,{"disambiguationData":[OSD([subQ0]),TDD([makeQuery(id+"F0.imprint","IMPRINT",EDGE,{"disambiguationData":[TD([[makeQuery(id+"F0.imprint","INTERSECT",VERTEX,{"derivedFrom":[sQuery(id+"F0.wireOp",EDGE,"E16.top"),subQ0]}),1.0]])],"derivedFrom":subQ0})])],"isStart":false});}
            var Q57;
            {var subQ0=sQuery(id+"F0.wireOp",EDGE,"E16.top");Q57=makeQuery(id+"F1.opExtrude","CAP_EDGE",EDGE,{"disambiguationData":[OSD([subQ0]),TDD([makeQuery(id+"F0.imprint","IMPRINT",EDGE,{"disambiguationData":[TD([[makeQuery(id+"F0.imprint","INTERSECT",VERTEX,{"derivedFrom":[subQ0,sQuery(id+"F0.wireOp",EDGE,"E16.left")]}),-1.0]])],"derivedFrom":subQ0})])],"isStart":false});}
            var Q58;
            Q58=makeQuery(id+"F1.opExtrude","CAP_EDGE",EDGE,{"disambiguationData":[OSD([sQuery(id+"F0.wireOp",EDGE,"E9.right")])],"isStart":false});
            var Q59;
            Q59=makeQuery(id+"F1.opExtrude","CAP_EDGE",EDGE,{"disambiguationData":[OSD([sQuery(id+"F0.wireOp",EDGE,"E13.right")])],"isStart":false});
            var Q60;
            Q60=makeQuery(id+"F1.opExtrude","CAP_EDGE",EDGE,{"disambiguationData":[OSD([sQuery(id+"F0.wireOp",EDGE,"E14.right")])],"isStart":false});
            var Q61;
            Q61=makeQuery(id+"F1.opExtrude","CAP_EDGE",EDGE,{"disambiguationData":[OSD([sQuery(id+"F0.wireOp",EDGE,"E15.right")])],"isStart":false});
            var Q62;
            Q62=makeQuery(id+"F1.opExtrude","CAP_EDGE",EDGE,{"disambiguationData":[OSD([sQuery(id+"F0.wireOp",EDGE,"E16.right")])],"isStart":false});
            var Q63;
            Q63=makeQuery(id+"F1.opExtrude","CAP_EDGE",EDGE,{"disambiguationData":[OSD([sQuery(id+"F0.wireOp",EDGE,"E17.left")])],"isStart":false});
            var Q64;
            Q64=makeQuery(id+"F1.opExtrude","CAP_EDGE",EDGE,{"disambiguationData":[OSD([sQuery(id+"F0.wireOp",EDGE,"E12.left")])],"isStart":false});
            var Q65;
            Q65=makeQuery(id+"F1.opExtrude","CAP_EDGE",EDGE,{"disambiguationData":[OSD([sQuery(id+"F0.wireOp",EDGE,"E11.left")])],"isStart":false});
            var Q66;
            Q66=makeQuery(id+"F1.opExtrude","CAP_EDGE",EDGE,{"disambiguationData":[OSD([sQuery(id+"F0.wireOp",EDGE,"E10.left")])],"isStart":false});
            var Q67;
            Q67=makeQuery(id+"F1.opExtrude","CAP_EDGE",EDGE,{"disambiguationData":[OSD([sQuery(id+"F0.wireOp",EDGE,"E9.left")])],"isStart":false});
            var Q68;
            Q68=makeQuery(id+"F1.opExtrude","CAP_EDGE",EDGE,{"disambiguationData":[OSD([sQuery(id+"F0.wireOp",EDGE,"E13.left")])],"isStart":false});
            var Q69;
            Q69=makeQuery(id+"F1.opExtrude","CAP_EDGE",EDGE,{"disambiguationData":[OSD([sQuery(id+"F0.wireOp",EDGE,"E14.left")])],"isStart":false});
            var Q70;
            Q70=makeQuery(id+"F1.opExtrude","CAP_EDGE",EDGE,{"disambiguationData":[OSD([sQuery(id+"F0.wireOp",EDGE,"E15.left")])],"isStart":false});
            var Q71;
            Q71=makeQuery(id+"F1.opExtrude","CAP_EDGE",EDGE,{"disambiguationData":[OSD([sQuery(id+"F0.wireOp",EDGE,"E16.left")])],"isStart":false});
            fillet(context, id + "F2", {"entities" : qUnion([Q0, Q1, Q2, Q3, Q4, Q5, Q6, Q7, Q8, Q9, Q10, Q11, Q12, Q13, Q14, Q15, Q16, Q17, Q18, Q19, Q20, Q21, Q22, Q23, Q24, Q25, Q26, Q27, Q28, Q29, Q30, Q31, Q32, Q33, Q34, Q35, Q36, Q37, Q38, Q39, Q40, Q41, Q42, Q43, Q44, Q45, Q46, Q47, Q48, Q49, Q50, Q51, Q52, Q53, Q54, Q55, Q56, Q57, Q58, Q59, Q60, Q61, Q62, Q63, Q64, Q65, Q66, Q67, Q68, Q69, Q70, Q71]), "radius" : .5 * mm, "tangentPropagation" : true, "allowEdgeOverflow" : false});
        }
        {
            var Q0;
            Q0=makeQuery(id+"F1.opExtrude","CAP_EDGE",EDGE,{"disambiguationData":[OSD([sQuery(id+"F0.wireOp",EDGE,"E8.bottom")])],"isStart":false});
            var Q1;
            Q1=makeQuery(id+"F1.opExtrude","CAP_EDGE",EDGE,{"disambiguationData":[OSD([sQuery(id+"F0.wireOp",EDGE,"E8.right")])],"isStart":false});
            var Q2;
            Q2=makeQuery(id+"F1.opExtrude","CAP_EDGE",EDGE,{"disambiguationData":[OSD([sQuery(id+"F0.wireOp",EDGE,"E8.top")])],"isStart":false});
            var Q3;
            Q3=makeQuery(id+"F1.opExtrude","CAP_EDGE",EDGE,{"disambiguationData":[OSD([sQuery(id+"F0.wireOp",EDGE,"E8.left")])],"isStart":false});
            fillet(context, id + "F3", {"entities" : qUnion([Q0, Q1, Q2, Q3]), "radius" : 1 * mm, "tangentPropagation" : true, "allowEdgeOverflow" : false});
        }
    });
